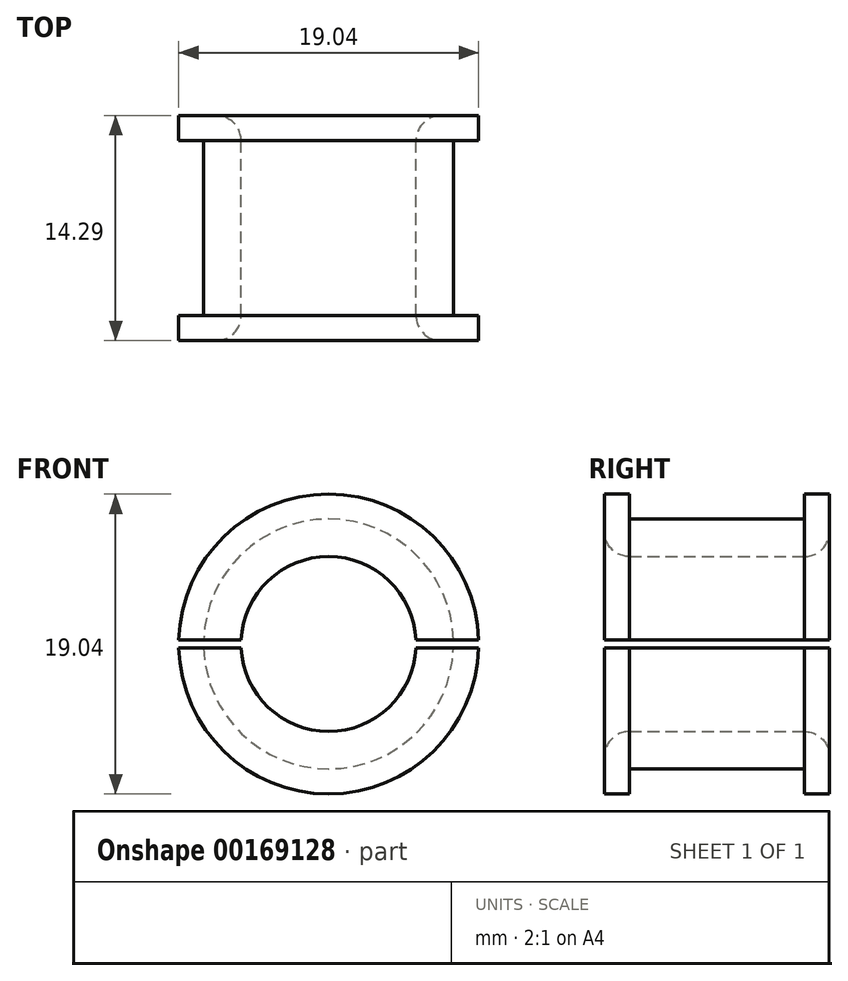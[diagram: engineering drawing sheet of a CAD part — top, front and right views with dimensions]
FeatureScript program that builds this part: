
annotation { "Feature Type Name" : "Feature", "Feature Type Description" : "" }
export const myFeature = defineFeature(function(context is Context, id is Id, definition is map)
    precondition{}
    {
        {
            var Q0;
            Q0=qCreatedBy(makeId("Front.planeOp"),FACE);
            var sketch = newSketch(context, id + "F0", { "sketchPlane" : qUnion([Q0])});
            skArc(sketch, "E0", {"start": v(9.52, 0.25) * mm, "mid": v(0, 9.53) * mm, "end": v(-9.52, 0.25) * mm});
            skArc(sketch, "E1", {"start": v(7.93, 0.25) * mm, "mid": v(0, 7.94) * mm, "end": v(-7.93, 0.25) * mm});
            skArc(sketch, "E2", {"start": v(5.55, 0.25) * mm, "mid": v(0, 5.56) * mm, "end": v(-5.55, 0.25) * mm});
            skLineSegment(sketch, "E3", {"start": v(-9.52, -0.25) * mm, "end": v(-5.55, -0.25) * mm});
            skLineSegment(sketch, "E4", {"start": v(9.52, 0.25) * mm, "end": v(5.55, 0.25) * mm});
            skArc(sketch, "E5.trimOffspring", {"start": v(-5.55, -0.25) * mm, "mid": v(0, -5.56) * mm, "end": v(5.55, -0.25) * mm});
            skLineSegment(sketch, "E6.trimOffspring", {"start": v(-5.55, 0.25) * mm, "end": v(-9.52, 0.25) * mm});
            skLineSegment(sketch, "E7.trimOffspring", {"start": v(5.55, -0.25) * mm, "end": v(9.52, -0.25) * mm});
            skArc(sketch, "E8.trimOffspring", {"start": v(-7.93, -0.25) * mm, "mid": v(0, -7.94) * mm, "end": v(7.93, -0.25) * mm});
            skArc(sketch, "E9.trimOffspring", {"start": v(-9.52, -0.25) * mm, "mid": v(0, -9.53) * mm, "end": v(9.52, -0.25) * mm});
            skSolve(sketch);
        }
        {
            var Q0;
            {var subQ0=sQuery(id+"F0.wireOp",EDGE,"E1");Q0=makeQuery(id+"F0.imprint","IMPRINT",FACE,{"disambiguationData":[TD([[makeQuery(id+"F0.imprint","IMPRINT",EDGE,{"derivedFrom":subQ0}),1.0]])]});}
            var Q1;
            {var subQ0=sQuery(id+"F0.wireOp",EDGE,"E5.trimOffspring");Q1=makeQuery(id+"F0.imprint","IMPRINT",FACE,{"disambiguationData":[TD([[makeQuery(id+"F0.imprint","IMPRINT",EDGE,{"derivedFrom":subQ0}),-1.0]])]});}
            extrude(context, id + "F1", {"entities" : qUnion([Q0, Q1]), "depth" : 11.1 * mm});
        }
        {
            var Q0;
            {var subQ0=sQuery(id+"F0.wireOp",EDGE,"E5.trimOffspring");Q0=makeQuery(id+"F0.imprint","IMPRINT",FACE,{"disambiguationData":[TD([[makeQuery(id+"F0.imprint","IMPRINT",EDGE,{"derivedFrom":subQ0}),-1.0]])]});}
            var Q1;
            {var subQ2=sQuery(id+"F0.wireOp",EDGE,"E8.trimOffspring");Q1=makeQuery(id+"F0.imprint","IMPRINT",FACE,{"disambiguationData":[TD([[makeQuery(id+"F0.imprint","IMPRINT",EDGE,{"derivedFrom":subQ2}),-1.0]])]});}
            var Q2;
            {var subQ0=sQuery(id+"F0.wireOp",EDGE,"E1");Q2=makeQuery(id+"F0.imprint","IMPRINT",FACE,{"disambiguationData":[TD([[makeQuery(id+"F0.imprint","IMPRINT",EDGE,{"derivedFrom":subQ0}),1.0]])]});}
            var Q3;
            {var subQ0=sQuery(id+"F0.wireOp",EDGE,"E0");Q3=makeQuery(id+"F0.imprint","IMPRINT",FACE,{"disambiguationData":[TD([[makeQuery(id+"F0.imprint","IMPRINT",EDGE,{"derivedFrom":subQ0}),1.0]])]});}
            extrude(context, id + "F2", {"entities" : qUnion([Q0, Q1, Q2, Q3]), "oppositeDirection" : true, "depth" : 1.59 * mm});
        }
        {
            var Q0;
            Q0 = qSketchRegion(id + "F0", true);
            extrude(context, id + "F3", {"entities" : qUnion([Q0]), "depth" : 12.7 * mm, "hasSecondDirection" : true, "secondDirectionOppositeDirection" : false, "secondDirectionDepth" : 11.1 * mm});
        }
        {
            var Q0;
            Q0=makeQuery(id+"F2.opExtrude","CAP_EDGE",EDGE,{"disambiguationData":[OSD([sQuery(id+"F0.wireOp",EDGE,"E2")])],"isStart":false});
            var Q1;
            Q1=makeQuery(id+"F2.opExtrude","CAP_EDGE",EDGE,{"disambiguationData":[OSD([sQuery(id+"F0.wireOp",EDGE,"E5.trimOffspring")])],"isStart":false});
            var Q2;
            Q2=makeQuery(id+"F3.opExtrude","CAP_EDGE",EDGE,{"disambiguationData":[OSD([sQuery(id+"F0.wireOp",EDGE,"E2")])],"isStart":false});
            var Q3;
            Q3=makeQuery(id+"F3.opExtrude","CAP_EDGE",EDGE,{"disambiguationData":[OSD([sQuery(id+"F0.wireOp",EDGE,"E5.trimOffspring")])],"isStart":false});
            fillet(context, id + "F4", {"entities" : qUnion([Q0, Q1, Q2, Q3]), "radius" : 1.59 * mm, "tangentPropagation" : true, "allowEdgeOverflow" : false});
        }
    });
